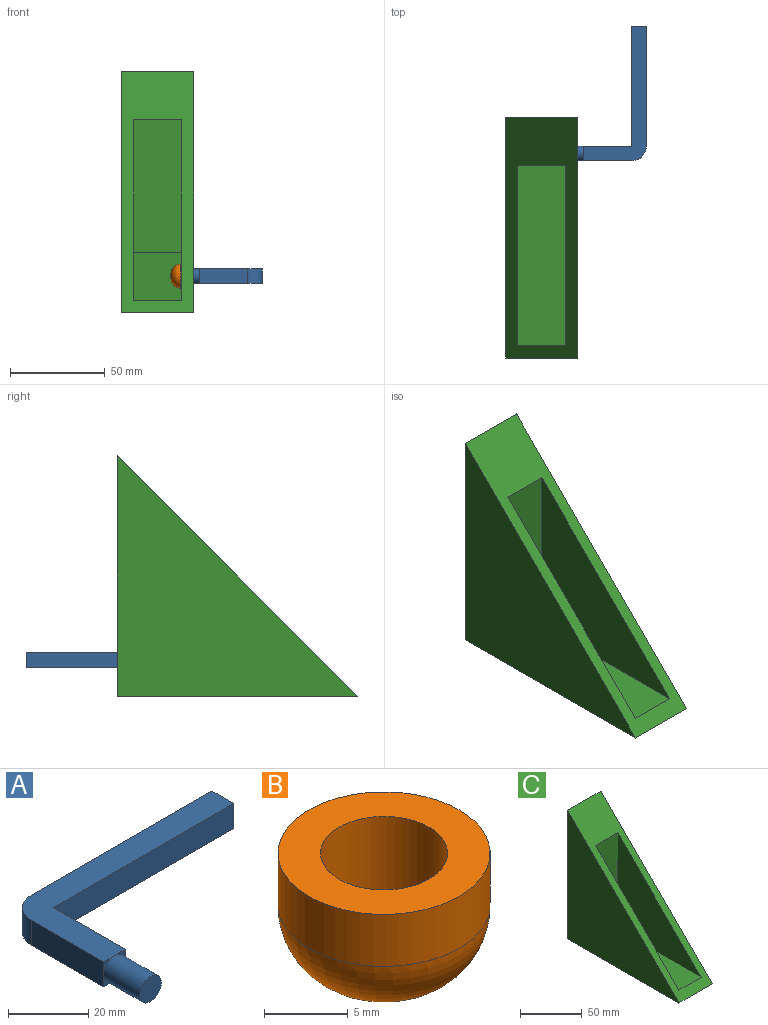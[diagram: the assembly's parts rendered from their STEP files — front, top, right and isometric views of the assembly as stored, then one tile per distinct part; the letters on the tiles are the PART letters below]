
ASSEMBLY  parts=3 mates=2
PART A: 14 faces, bbox 71.1x45.7x7.6 mm
  f0: plane 3.81x3.81mm, normal (0,-1,0), area 3.1mm2, adj f3,f9,f11
  f1: plane 3.81x3.81mm, normal (0,-1,0), area 3.1mm2, adj f3,f8,f11
  f2: plane 3.81x3.81mm, normal (0,-1,0), area 3.1mm2, adj f7,f8,f11
  f3: plane 25.4x7.62mm, normal (1,0,0), area 193.5mm2, adj f0,f1,f4,f8,f9
  f4: plane 63.5x7.62mm, normal (0,-1,0), area 483.9mm2, adj f3,f8,f9,f13
  f5: plane 63.5x7.62mm, normal (0,1,0), area 483.9mm2, adj f6,f8,f9,f13
  f6: cylinder r=7.62mm len=7.62mm, axis (0,0,-1), area 91.2mm2, adj f5,f7,f8,f9
  f7: plane 25.4x7.62mm, normal (-1,0,0), area 193.5mm2, adj f2,f6,f8,f9,f10
  f8: plane 71.12x33.02mm, normal (0,0,1), area 723mm2, adj f1,f2,f3,f4,f5,f6,f7,f13
  f9: plane 71.12x33.02mm, normal (0,0,-1), area 723mm2, adj f0,f3,f4,f5,f6,f7,f10,f13
  f10: plane 3.81x3.81mm, normal (0,-1,0), area 3.1mm2, adj f7,f9,f11
  f11: cylinder r=3.81mm len=12.7mm, axis (0,1,0), area 304mm2, adj f0,f1,f2,f10,f12
  f12: plane 7.62x7.62mm, normal (0,-1,0), area 45.6mm2, adj f11
  f13: plane 7.62x7.62mm, normal (1,0,0), area 58.1mm2, adj f4,f5,f8,f9
PART B: 6 faces, bbox 12.7x12.7x8.9 mm
  f0: cylinder r=6.35mm len=12.7mm, axis (0,0,-1), area 152mm2, adj f1,f5
  f1: plane 12.7x12.7mm, normal (0,0,1), area 81.1mm2, adj f0,f3
  f2: plane 2.54x2.54mm, normal (0,0,-1), area 5.1mm2, adj f5
  f3: cylinder r=3.81mm len=7.62mm, axis (0,0,1), area 152mm2, adj f1,f4
  f4: plane 7.62x7.62mm, normal (0,0,1), area 45.6mm2, adj f3
  f5: torus R=1.27mm, axis (0,0,1), area 225.8mm2, adj f0,f2
PART C: 12 faces, bbox 38.1x127x127 mm
  f0: plane 69.85x25.4mm, normal (0,-1,0), area 1774.2mm2, adj f1,f2,f4,f10
  f1: plane 114.3x95.25mm, normal (1,0,0), area 5020.2mm2, adj f0,f3,f4,f10,f11
  f2: plane 114.3x95.25mm, normal (-1,0,0), area 4974.5mm2, adj f0,f3,f4,f9,f10,f11
  f3: plane 114.3x25.4mm, normal (0,0,1), area 2903.2mm2, adj f1,f2,f4,f11
  f4: plane 127x127mm, normal (0,-0.71,0.71), area 3421.5mm2, adj f0,f1,f2,f3,f5,f6,f7,f8
  f5: plane 127x127mm, normal (1,0,0), area 8018.9mm2, adj f4,f6,f8,f9
  f6: plane 127x38.1mm, normal (0,1,0), area 4838.7mm2, adj f4,f5,f7,f8
  f7: plane 127x127mm, normal (-1,0,0), area 8064.5mm2, adj f4,f6,f8
  f8: plane 127x38.1mm, normal (0,0,-1), area 4838.7mm2, adj f4,f5,f6,f7
  f9: cylinder r=3.81mm len=7.62mm, axis (1,0,0), area 152mm2, adj f2,f5
  f10: plane 25.4x19.05mm, normal (0,0,-1), area 483.9mm2, adj f0,f1,f2,f11
  f11: plane 25.4x25.4mm, normal (0,-1,0), area 645.2mm2, adj f1,f2,f3,f10
PLACE A rot(axis=(0.71,0.71,0),180deg) t=(144.8,132.64,21.51)mm
PLACE B rot(axis=(-0.58,0.58,-0.58),120deg) t=(142.26,128.83,17.7)mm
PLACE C t=(154.34,20.88,-1.35)mm
MATE slider C.f9 <-> A.f11  axis (1,0,0) through (154.34,128.83,17.7)mm
MATE fastened B.f3 <-> A.f11  axis (1,0,0) through (144.8,128.83,17.7)mm
